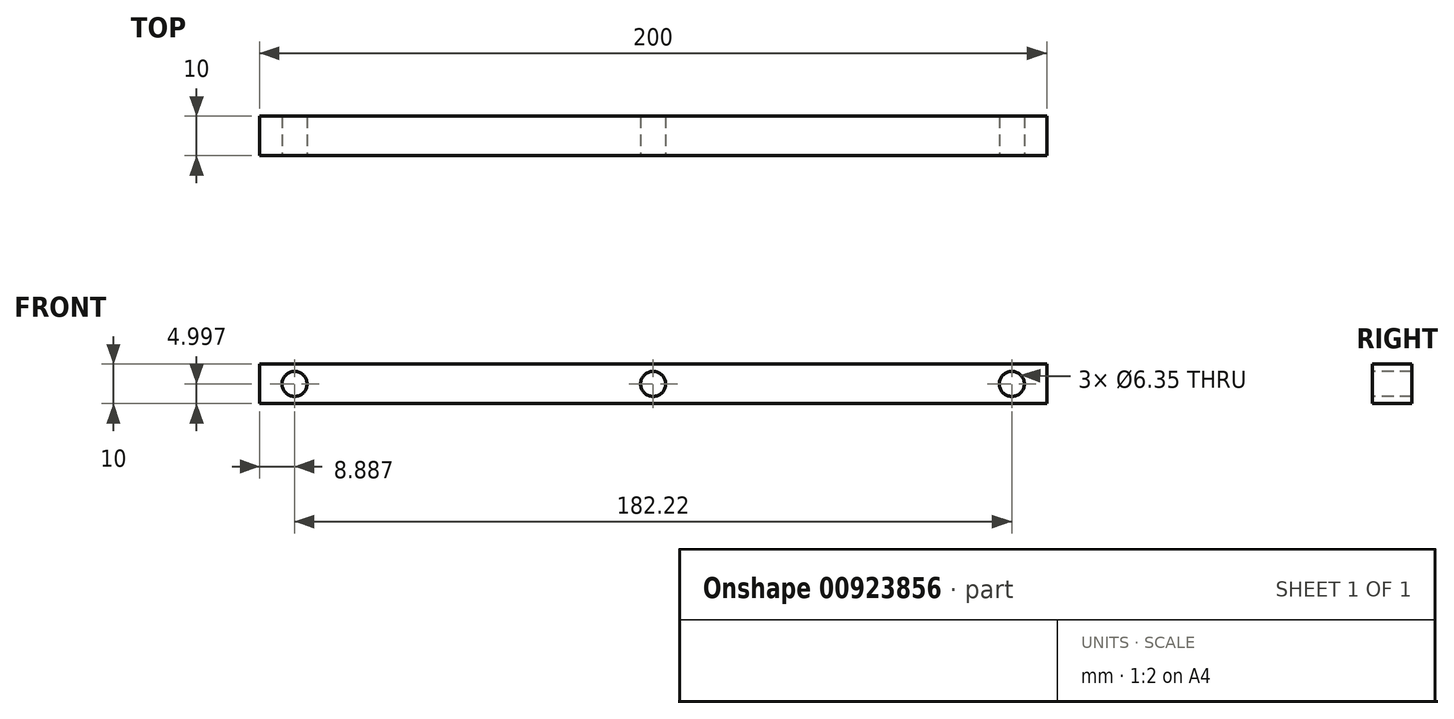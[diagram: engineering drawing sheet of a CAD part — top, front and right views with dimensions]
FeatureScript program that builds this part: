
annotation { "Feature Type Name" : "Feature", "Feature Type Description" : "" }
export const myFeature = defineFeature(function(context is Context, id is Id, definition is map)
    precondition{}
    {
        {
            var Q0;
            Q0=qCreatedBy(makeId("Front.planeOp"),FACE);
            var sketch = newSketch(context, id + "F0", { "sketchPlane" : qUnion([Q0])});
            skLineSegment(sketch, "E0.bottom", {"start": v(-150.9, -6.05) * mm, "end": v(49.1, -6.05) * mm});
            skLineSegment(sketch, "E0.top", {"start": v(-150.9, -16.05) * mm, "end": v(49.1, -16.05) * mm});
            skLineSegment(sketch, "E0.left", {"start": v(-150.9, -6.05) * mm, "end": v(-150.9, -16.05) * mm});
            skLineSegment(sketch, "E0.right", {"start": v(49.1, -6.05) * mm, "end": v(49.1, -16.05) * mm});
            skSolve(sketch);
        }
        {
            var Q0;
            Q0=makeQuery(id+"F0.imprint","IMPRINT",FACE,{"disambiguationData":[TD([[makeQuery(id+"F0.imprint","IMPRINT",EDGE,{"derivedFrom":sQuery(id+"F0.wireOp",EDGE,"E0.bottom")}),-1.0]])]});
            extrude(context, id + "F1", {"entities" : qUnion([Q0]), "depth" : 10 * mm, "offsetDistance" : 25.4 * mm});
        }
        {
            var Q0;
            Q0=makeQuery(id+"F1.opExtrude","CAP_FACE",FACE,{"disambiguationData":[OSD([sQuery(id+"F0.wireOp",EDGE,"E0.bottom"),sQuery(id+"F0.wireOp",EDGE,"E0.top"),sQuery(id+"F0.wireOp",EDGE,"E0.left"),sQuery(id+"F0.wireOp",EDGE,"E0.right")])],"isStart":false});
            var sketch = newSketch(context, id + "F2", { "sketchPlane" : qUnion([Q0])});
            skCircle(sketch, "E1", {"center": v(-142.01, -11.05) * mm, "radius": 3.18 * mm});
            skSolve(sketch);
        }
        {
            var Q0;
            Q0=sQuery(id+"F2.wireOp",VERTEX,"E1.center");
            var Q1;
            Q1=makeQuery(id+"F1.opExtrude","SWEPT_BODY",BODY,{"disambiguationData":[OSD([sQuery(id+"F0.wireOp",EDGE,"E0.bottom"),sQuery(id+"F0.wireOp",EDGE,"E0.top"),sQuery(id+"F0.wireOp",EDGE,"E0.left"),sQuery(id+"F0.wireOp",EDGE,"E0.right")])]});
            hole(context, id + "F3", {"style" : HoleStyle.SIMPLE, "endStyle" : HoleEndStyle.THROUGH, "holeDiameter" : 6.35 * mm, "majorDiameter" : 6.35 * mm, "isTappedThrough" : true, "tappedDepth" : 12.7 * mm, "tapClearance" : 3, "locations" : qUnion([Q0]), "scope" : qUnion([Q1])});
        }
        {
            var Q0;
            Q0=makeQuery(id+"F1.opExtrude","CAP_FACE",FACE,{"disambiguationData":[OSD([sQuery(id+"F0.wireOp",EDGE,"E0.bottom"),sQuery(id+"F0.wireOp",EDGE,"E0.top"),sQuery(id+"F0.wireOp",EDGE,"E0.left"),sQuery(id+"F0.wireOp",EDGE,"E0.right")])],"isStart":false});
            var sketch = newSketch(context, id + "F4", { "sketchPlane" : qUnion([Q0])});
            skCircle(sketch, "E2", {"center": v(40.2, -11.05) * mm, "radius": 3.18 * mm});
            skSolve(sketch);
        }
        {
            var Q0;
            Q0=sQuery(id+"F4.wireOp",VERTEX,"E2.center");
            var Q1;
            Q1=makeQuery(id+"F1.opExtrude","SWEPT_BODY",BODY,{"disambiguationData":[OSD([sQuery(id+"F0.wireOp",EDGE,"E0.bottom"),sQuery(id+"F0.wireOp",EDGE,"E0.top"),sQuery(id+"F0.wireOp",EDGE,"E0.left"),sQuery(id+"F0.wireOp",EDGE,"E0.right")])]});
            hole(context, id + "F5", {"style" : HoleStyle.SIMPLE, "endStyle" : HoleEndStyle.THROUGH, "holeDiameter" : 6.35 * mm, "majorDiameter" : 6.35 * mm, "isTappedThrough" : true, "tappedDepth" : 12.7 * mm, "tapClearance" : 3, "locations" : qUnion([Q0]), "scope" : qUnion([Q1])});
        }
        {
            var Q0;
            Q0=makeQuery(id+"F1.opExtrude","CAP_FACE",FACE,{"disambiguationData":[OSD([sQuery(id+"F0.wireOp",EDGE,"E0.bottom"),sQuery(id+"F0.wireOp",EDGE,"E0.top"),sQuery(id+"F0.wireOp",EDGE,"E0.left"),sQuery(id+"F0.wireOp",EDGE,"E0.right")])],"isStart":false});
            var sketch = newSketch(context, id + "F6", { "sketchPlane" : qUnion([Q0])});
            skCircle(sketch, "E3", {"center": v(-50.9, -11.05) * mm, "radius": 3.18 * mm});
            skSolve(sketch);
        }
        {
            var Q0;
            Q0=sQuery(id+"F6.wireOp",VERTEX,"E3.center");
            var Q1;
            Q1=makeQuery(id+"F1.opExtrude","SWEPT_BODY",BODY,{"disambiguationData":[OSD([sQuery(id+"F0.wireOp",EDGE,"E0.bottom"),sQuery(id+"F0.wireOp",EDGE,"E0.top"),sQuery(id+"F0.wireOp",EDGE,"E0.left"),sQuery(id+"F0.wireOp",EDGE,"E0.right")])]});
            hole(context, id + "F7", {"style" : HoleStyle.SIMPLE, "endStyle" : HoleEndStyle.THROUGH, "holeDiameter" : 6.35 * mm, "majorDiameter" : 6.35 * mm, "isTappedThrough" : true, "tappedDepth" : 12.7 * mm, "tapClearance" : 3, "locations" : qUnion([Q0]), "scope" : qUnion([Q1])});
        }
    });
